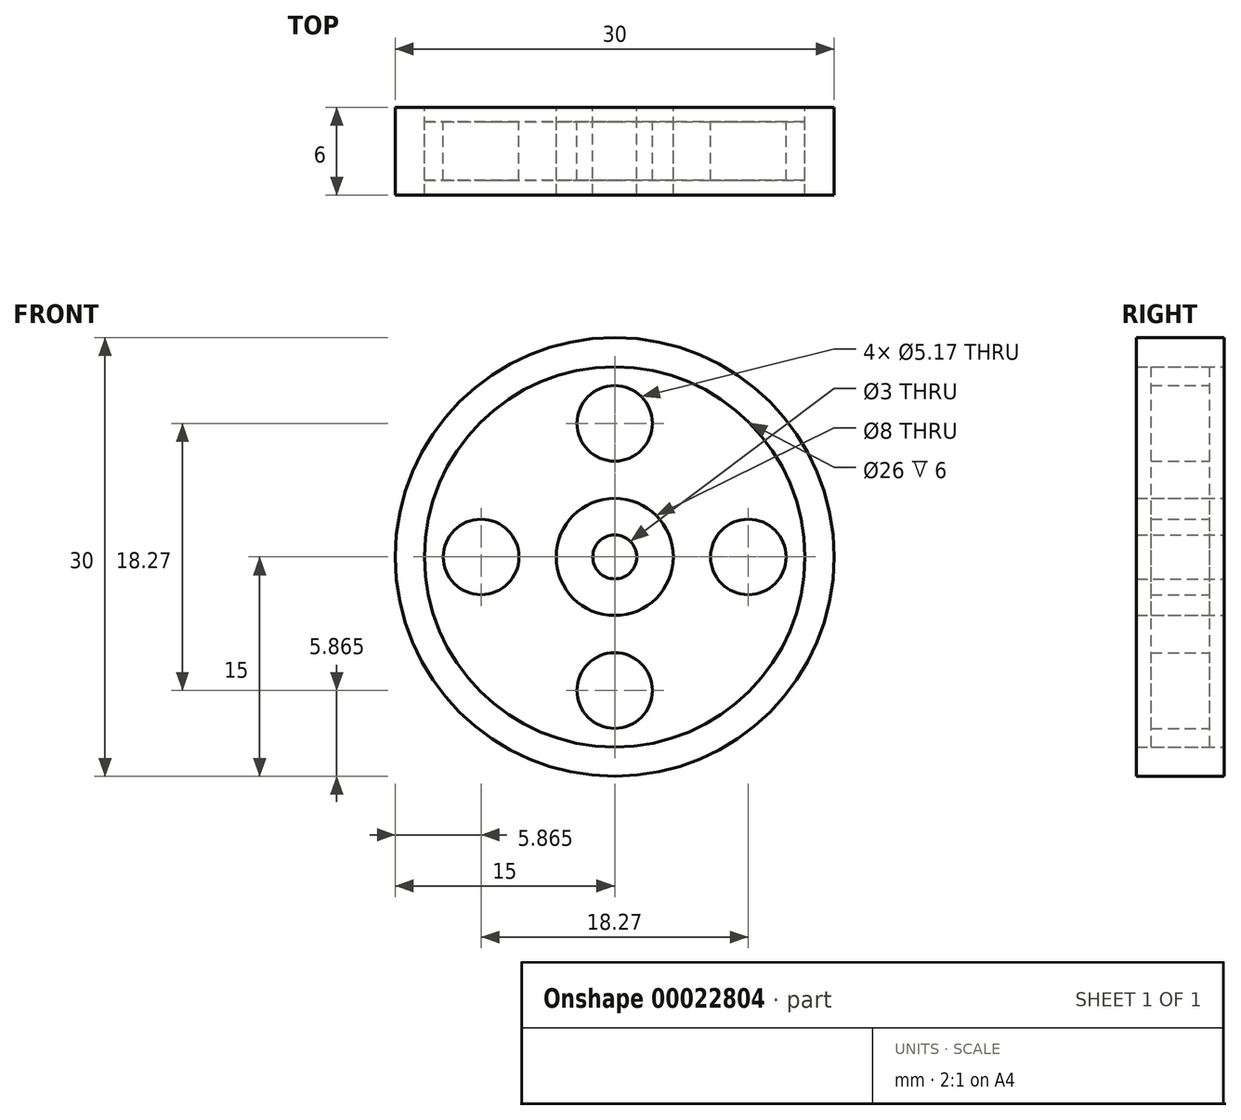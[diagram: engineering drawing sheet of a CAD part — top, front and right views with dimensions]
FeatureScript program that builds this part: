
annotation { "Feature Type Name" : "Feature", "Feature Type Description" : "" }
export const myFeature = defineFeature(function(context is Context, id is Id, definition is map)
    precondition{}
    {
        {
            var Q0;
            Q0=qCreatedBy(makeId("Front.planeOp"),FACE);
            var sketch = newSketch(context, id + "F0", { "sketchPlane" : qUnion([Q0])});
            skCircle(sketch, "E0", {"center": v(0, 0) * mm, "radius": 13 * mm});
            skCircle(sketch, "E1", {"center": v(0, 9.13) * mm, "radius": 2.58 * mm});
            skCircle(sketch, "E2.1.0", {"center": v(-9.13, 0) * mm, "radius": 2.58 * mm});
            skCircle(sketch, "E2.2.0", {"center": v(0, -9.13) * mm, "radius": 2.58 * mm});
            skCircle(sketch, "E2.3.0", {"center": v(9.13, 0) * mm, "radius": 2.58 * mm});
            skCircle(sketch, "E3", {"center": v(0, 0) * mm, "radius": 1.5 * mm});
            skCircle(sketch, "E4", {"center": v(0, 0) * mm, "radius": 4 * mm});
            skCircle(sketch, "E5", {"center": v(0, 0) * mm, "radius": 15 * mm});
            skSolve(sketch);
        }
        {
            var Q0;
            Q0=makeQuery(id+"F0.imprint","IMPRINT",FACE,{"disambiguationData":[TD([[makeQuery(id+"F0.imprint","IMPRINT",EDGE,{"derivedFrom":sQuery(id+"F0.wireOp",EDGE,"E0")}),-1.0]])]});
            extrude(context, id + "F1", {"entities" : qUnion([Q0]), "endBound" : BoundingType.SYMMETRIC, "depth" : 6 * mm});
        }
        {
            var Q0;
            Q0=makeQuery(id+"F0.imprint","IMPRINT",FACE,{"disambiguationData":[TD([[makeQuery(id+"F0.imprint","IMPRINT",EDGE,{"derivedFrom":sQuery(id+"F0.wireOp",EDGE,"E3")}),-1.0]])]});
            extrude(context, id + "F2", {"entities" : qUnion([Q0]), "endBound" : BoundingType.SYMMETRIC, "depth" : 6 * mm});
        }
        {
            var Q0;
            Q0=makeQuery(id+"F0.imprint","IMPRINT",FACE,{"disambiguationData":[TD([[makeQuery(id+"F0.imprint","IMPRINT",EDGE,{"derivedFrom":sQuery(id+"F0.wireOp",EDGE,"E0")}),1.0]])]});
            extrude(context, id + "F3", {"entities" : qUnion([Q0]), "endBound" : BoundingType.SYMMETRIC, "depth" : 4 * mm});
        }
    });
